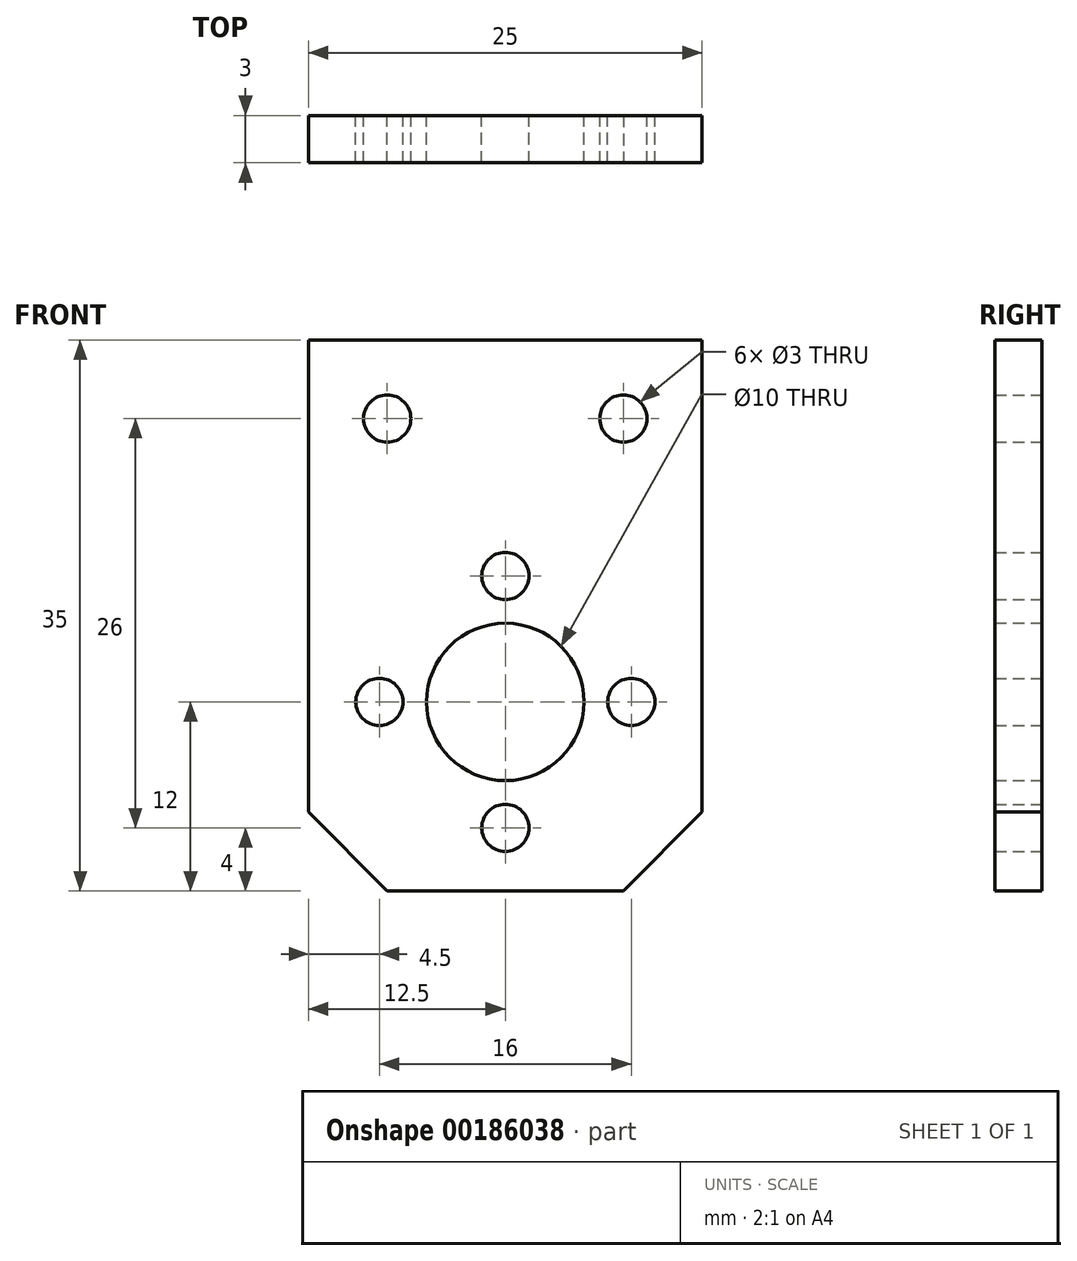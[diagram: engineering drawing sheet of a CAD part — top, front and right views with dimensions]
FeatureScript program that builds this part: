
annotation { "Feature Type Name" : "Feature", "Feature Type Description" : "" }
export const myFeature = defineFeature(function(context is Context, id is Id, definition is map)
    precondition{}
    {
        {
            var Q0;
            Q0=qCreatedBy(makeId("Front.planeOp"),FACE);
            var sketch = newSketch(context, id + "F0", { "sketchPlane" : qUnion([Q0])});
            skLineSegment(sketch, "E0.top", {"start": v(-12.5, 23) * mm, "end": v(12.5, 23) * mm});
            skLineSegment(sketch, "E0.left", {"start": v(-12.5, -12) * mm, "end": v(-12.5, 23) * mm});
            skLineSegment(sketch, "E0.right", {"start": v(12.5, -12) * mm, "end": v(12.5, 23) * mm});
            skPoint(sketch, "E0.middle", {"position": v(0, 0) * mm});
            skCircle(sketch, "E1", {"center": v(0, 0) * mm, "radius": 5 * mm});
            skCircle(sketch, "E2", {"center": v(0, 8) * mm, "radius": 1.5 * mm});
            skCircle(sketch, "E3.1.0", {"center": v(-8, 0) * mm, "radius": 1.5 * mm});
            skCircle(sketch, "E3.2.0", {"center": v(0, -8) * mm, "radius": 1.5 * mm});
            skCircle(sketch, "E3.3.0", {"center": v(8, 0) * mm, "radius": 1.5 * mm});
            skCircle(sketch, "E4", {"center": v(-7.5, 18) * mm, "radius": 1.5 * mm});
            skLineSegment(sketch, "E5", {"start": v(-12.5, 0) * mm, "end": v(12.5, 0) * mm, "construction": true});
            skCircle(sketch, "E6", {"center": v(0, 0) * mm, "radius": 11 * mm, "construction": true});
            skLineSegment(sketch, "E7", {"start": v(-12.5, -12) * mm, "end": v(12.5, -12) * mm});
            skLineSegment(sketch, "E8", {"start": v(0, 23) * mm, "end": v(0, -12) * mm, "construction": true});
            skCircle(sketch, "E9.MirrorC", {"center": v(7.5, 18) * mm, "radius": 1.5 * mm});
            skSolve(sketch);
        }
        {
            var Q0;
            Q0 = qSketchRegion(id + "F0", true);
            extrude(context, id + "F1", {"entities" : qUnion([Q0]), "depth" : 3 * mm});
        }
        {
            var Q0;
            Q0=makeQuery(id+"F1.opExtrude","SWEPT_EDGE",EDGE,{"disambiguationData":[OSD([sQuery(id+"F0.wireOp",EDGE,"E0.left"),sQuery(id+"F0.wireOp",EDGE,"E7")])]});
            var Q1;
            Q1=makeQuery(id+"F1.opExtrude","SWEPT_EDGE",EDGE,{"disambiguationData":[OSD([sQuery(id+"F0.wireOp",EDGE,"E0.right"),sQuery(id+"F0.wireOp",EDGE,"E7")])]});
            chamfer(context, id + "F2", {"entities" : qUnion([Q0, Q1]), "width" : 5 * mm, "tangentPropagation" : true});
        }
    });
